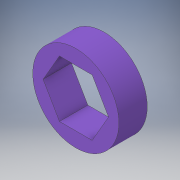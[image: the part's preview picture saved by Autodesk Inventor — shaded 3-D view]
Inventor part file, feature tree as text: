
AUTODESK INVENTOR PART (.ipt)
format: ipt  version: 2018 (Build 220112000, 112)  size: 108,544 bytes
history: native  units: in
note: dims shown in document units (in); Inventor stores cm internally (conversion verified against a paired STEP export)
features: extrude x1, sketch x1
ambient origin geometry x8: Origin, YZ Plane, XZ Plane, XY Plane, X Axis, Y Axis, Z Axis, Center Point
bodies: Solid1 (feature_tree)
feature tree (2):
  extrude  "Extrusion1"  Depth=0.5in
  sketch  "Sketch1"  dims[d0=0.76in d1=0.5in d2=0.25in d3=0.0in]
